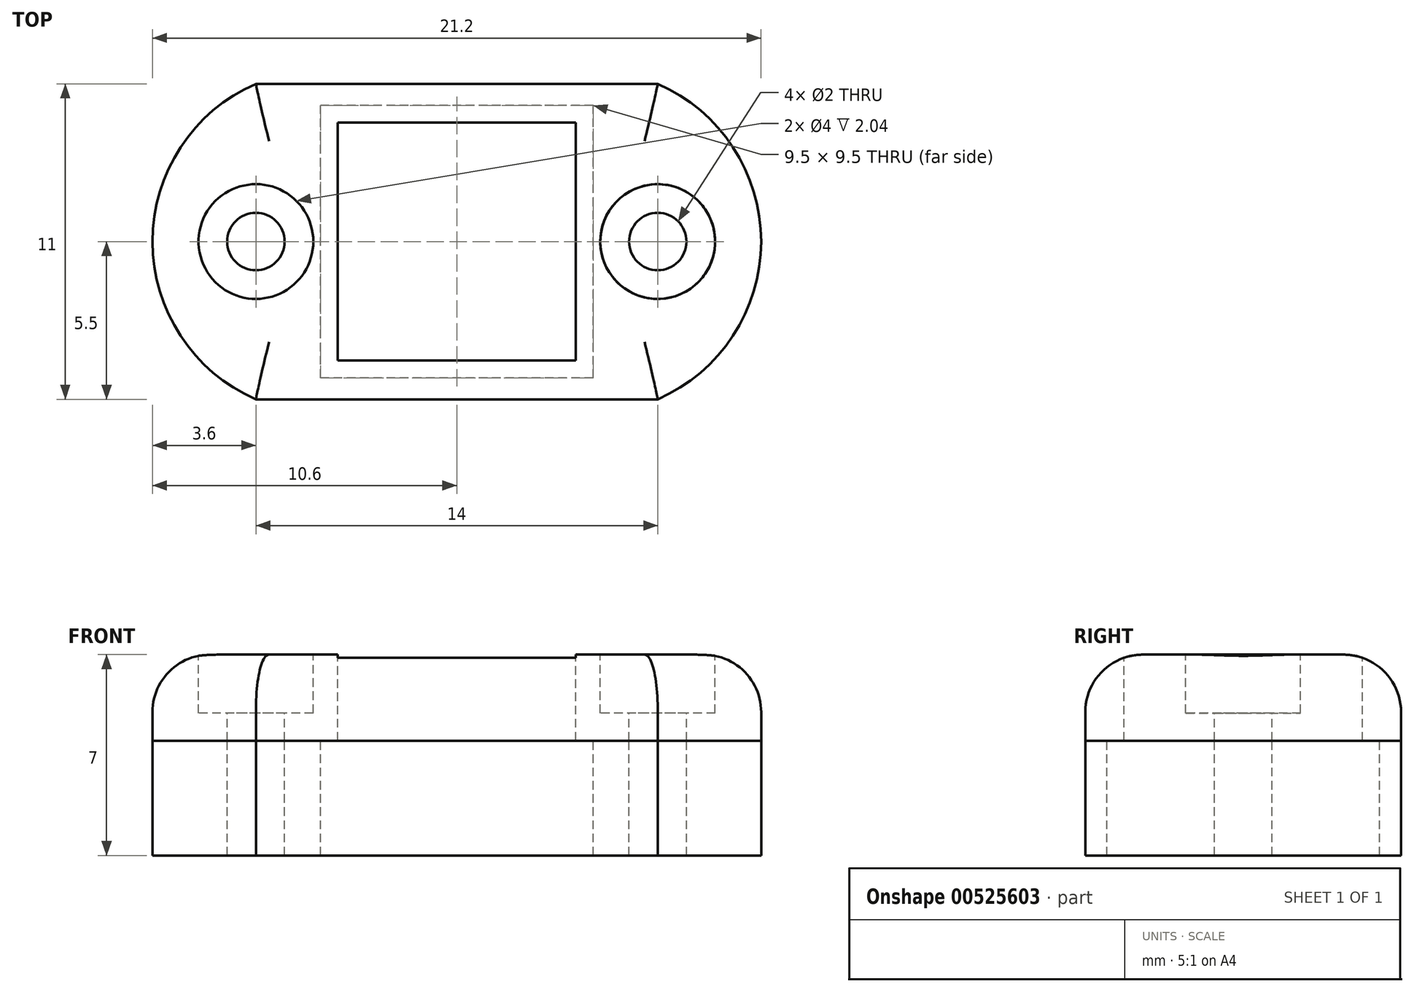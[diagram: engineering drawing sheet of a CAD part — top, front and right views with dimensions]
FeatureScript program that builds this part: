
annotation { "Feature Type Name" : "Feature", "Feature Type Description" : "" }
export const myFeature = defineFeature(function(context is Context, id is Id, definition is map)
    precondition{}
    {
        {
            var Q0;
            Q0=qCreatedBy(makeId("Top.planeOp"),FACE);
            var sketch = newSketch(context, id + "F0", { "sketchPlane" : qUnion([Q0])});
            skLineSegment(sketch, "E0.top", {"start": v(7, 5.5) * mm, "end": v(-7, 5.5) * mm});
            skLineSegment(sketch, "E0.left", {"start": v(7, -5.5) * mm, "end": v(7, 5.5) * mm});
            skLineSegment(sketch, "E0.right", {"start": v(-7, -5.5) * mm, "end": v(-7, 5.5) * mm});
            skPoint(sketch, "E0.middle", {"position": v(0, 0) * mm});
            skArc(sketch, "E1", {"start": v(7, -5.5) * mm, "mid": v(10.6, 0) * mm, "end": v(7, 5.5) * mm});
            skArc(sketch, "E2", {"start": v(-7, 5.5) * mm, "mid": v(-10.6, 0) * mm, "end": v(-7, -5.5) * mm});
            skLineSegment(sketch, "E3", {"start": v(-7, -5.5) * mm, "end": v(7, -5.5) * mm});
            skSolve(sketch);
        }
        {
            var Q0;
            Q0=qSketchRegion(id+"F0",true);
            extrude(context, id + "F1", {"entities" : qUnion([Q0]), "depth" : 4 * mm, "offsetDistance" : 25 * mm});
        }
        {
            var Q0;
            Q0=makeQuery(id+"F1.opExtrude","CAP_FACE",FACE,{"disambiguationData":[OSD([sQuery(id+"F0.wireOp",EDGE,"E0.bottom"),sQuery(id+"F0.wireOp",EDGE,"E0.top"),sQuery(id+"F0.wireOp",EDGE,"E0.left"),sQuery(id+"F0.wireOp",EDGE,"E0.right")])],"isStart":false});
            var sketch = newSketch(context, id + "F2", { "sketchPlane" : qUnion([Q0])});
            skCircle(sketch, "E4", {"center": v(-7, 0) * mm, "radius": 1 * mm});
            skCircle(sketch, "E5", {"center": v(7, 0) * mm, "radius": 1 * mm});
            skCircle(sketch, "E6", {"center": v(0, 0) * mm, "radius": 3.55 * mm, "construction": true});
            skLineSegment(sketch, "E7.bottom", {"start": v(4.75, -4.75) * mm, "end": v(-4.75, -4.75) * mm});
            skLineSegment(sketch, "E7.top", {"start": v(4.75, 4.75) * mm, "end": v(-4.75, 4.75) * mm});
            skLineSegment(sketch, "E7.left", {"start": v(4.75, -4.75) * mm, "end": v(4.75, 4.75) * mm});
            skLineSegment(sketch, "E7.right", {"start": v(-4.75, -4.75) * mm, "end": v(-4.75, 4.75) * mm});
            skSolve(sketch);
        }
        {
            var Q0;
            Q0=qSketchRegion(id+"F2",true);
            extrude(context, id + "F3", {"entities" : qUnion([Q0]), "operationType" : NewBodyOperationType.REMOVE, "oppositeDirection" : true, "depth" : 5 * mm});
        }
        {
            var Q0;
            Q0=makeQuery(id+"F1.opExtrude","CAP_FACE",FACE,{"disambiguationData":[OSD([sQuery(id+"F0.wireOp",EDGE,"E0.top"),sQuery(id+"F0.wireOp",EDGE,"E1"),sQuery(id+"F0.wireOp",EDGE,"E2"),sQuery(id+"F0.wireOp",EDGE,"E3")])],"isStart":false});
            var sketch = newSketch(context, id + "F4", { "sketchPlane" : qUnion([Q0])});
            skLineSegment(sketch, "E8.top", {"start": v(7, 5.5) * mm, "end": v(-7, 5.5) * mm});
            skLineSegment(sketch, "E8.left", {"start": v(7, -5.5) * mm, "end": v(7, 5.5) * mm});
            skLineSegment(sketch, "E8.right", {"start": v(-7, -5.5) * mm, "end": v(-7, 5.5) * mm});
            skPoint(sketch, "E8.middle", {"position": v(0, 0) * mm});
            skArc(sketch, "E9", {"start": v(7, -5.5) * mm, "mid": v(10.6, 0) * mm, "end": v(7, 5.5) * mm});
            skArc(sketch, "E10", {"start": v(-7, 5.5) * mm, "mid": v(-10.6, 0) * mm, "end": v(-7, -5.5) * mm});
            skLineSegment(sketch, "E11", {"start": v(-7, -5.5) * mm, "end": v(7, -5.5) * mm});
            skPoint(sketch, "E12", {"position": v(4.75, 0) * mm});
            skPoint(sketch, "E13", {"position": v(0, 4.75) * mm});
            skSolve(sketch);
        }
        {
            var Q0;
            Q0=qSketchRegion(id+"F4",true);
            extrude(context, id + "F5", {"entities" : qUnion([Q0]), "depth" : 3 * mm, "offsetDistance" : 25 * mm});
        }
        {
            var Q0;
            Q0=makeQuery(id+"F5.opExtrude","CAP_FACE",FACE,{"disambiguationData":[OSD([sQuery(id+"F4.wireOp",EDGE,"E8.top"),sQuery(id+"F4.wireOp",EDGE,"E9"),sQuery(id+"F4.wireOp",EDGE,"E10"),sQuery(id+"F4.wireOp",EDGE,"E11")])],"isStart":false});
            var sketch = newSketch(context, id + "F6", { "sketchPlane" : qUnion([Q0])});
            skCircle(sketch, "E14", {"center": v(-7, 0) * mm, "radius": 1 * mm, "construction": true});
            skCircle(sketch, "E15", {"center": v(7, 0) * mm, "radius": 1 * mm, "construction": true});
            skCircle(sketch, "E16", {"center": v(0, 0) * mm, "radius": 3.55 * mm, "construction": true});
            skPoint(sketch, "E17", {"position": v(-1.4, 0) * mm});
            skPoint(sketch, "E18", {"position": v(0, -5.5) * mm});
            skLineSegment(sketch, "E19.bottom", {"start": v(4.15, -4.15) * mm, "end": v(-4.15, -4.15) * mm});
            skLineSegment(sketch, "E19.top", {"start": v(4.15, 4.15) * mm, "end": v(-4.15, 4.15) * mm});
            skLineSegment(sketch, "E19.left", {"start": v(4.15, -4.15) * mm, "end": v(4.15, 4.15) * mm});
            skLineSegment(sketch, "E19.right", {"start": v(-4.15, -4.15) * mm, "end": v(-4.15, 4.15) * mm});
            skSolve(sketch);
        }
        {
            var Q0;
            Q0=qSketchRegion(id+"F6",true);
            extrude(context, id + "F7", {"entities" : qUnion([Q0]), "operationType" : NewBodyOperationType.REMOVE, "oppositeDirection" : true, "depth" : 3 * mm, "offsetDistance" : 25 * mm});
        }
        {
            var Q0;
            Q0=makeQuery(id+"F5.opExtrude","CAP_EDGE",EDGE,{"disambiguationData":[OSD([sQuery(id+"F4.wireOp",EDGE,"E9")])],"isStart":false});
            var Q1;
            Q1=makeQuery(id+"F5.opExtrude","CAP_EDGE",EDGE,{"disambiguationData":[OSD([sQuery(id+"F4.wireOp",EDGE,"E8.top")])],"isStart":false});
            var Q2;
            Q2=makeQuery(id+"F5.opExtrude","CAP_EDGE",EDGE,{"disambiguationData":[OSD([sQuery(id+"F4.wireOp",EDGE,"E10")])],"isStart":false});
            var Q3;
            Q3=makeQuery(id+"F5.opExtrude","CAP_EDGE",EDGE,{"disambiguationData":[OSD([sQuery(id+"F4.wireOp",EDGE,"E11")])],"isStart":false});
            fillet(context, id + "F8", {"entities" : qUnion([Q0, Q1, Q2, Q3]), "radius" : 2 * mm, "tangentPropagation" : true, "allowEdgeOverflow" : false});
        }
        {
            var Q0;
            Q0=sQuery(id+"F6.wireOp",VERTEX,"E15.center");
            var Q1;
            Q1=sQuery(id+"F6.wireOp",VERTEX,"E14.center");
            var Q2;
            Q2=makeQuery(id+"F5.opExtrude","SWEPT_BODY",BODY,{"disambiguationData":[OSD([sQuery(id+"F4.wireOp",EDGE,"E8.top"),sQuery(id+"F4.wireOp",EDGE,"E9"),sQuery(id+"F4.wireOp",EDGE,"E10"),sQuery(id+"F4.wireOp",EDGE,"E11")])]});
            hole(context, id + "F9", {"style" : HoleStyle.C_BORE, "endStyle" : HoleEndStyle.BLIND, "holeDiameter" : 2 * mm, "cBoreDiameter" : 4 * mm, "cBoreDepth" : 2 * mm, "majorDiameter" : 5 * mm, "holeDepth" : 20 * mm, "tappedDepth" : 12 * mm, "tapClearance" : 3, "locations" : qUnion([Q0, Q1]), "scope" : qUnion([Q2])});
        }
    });
